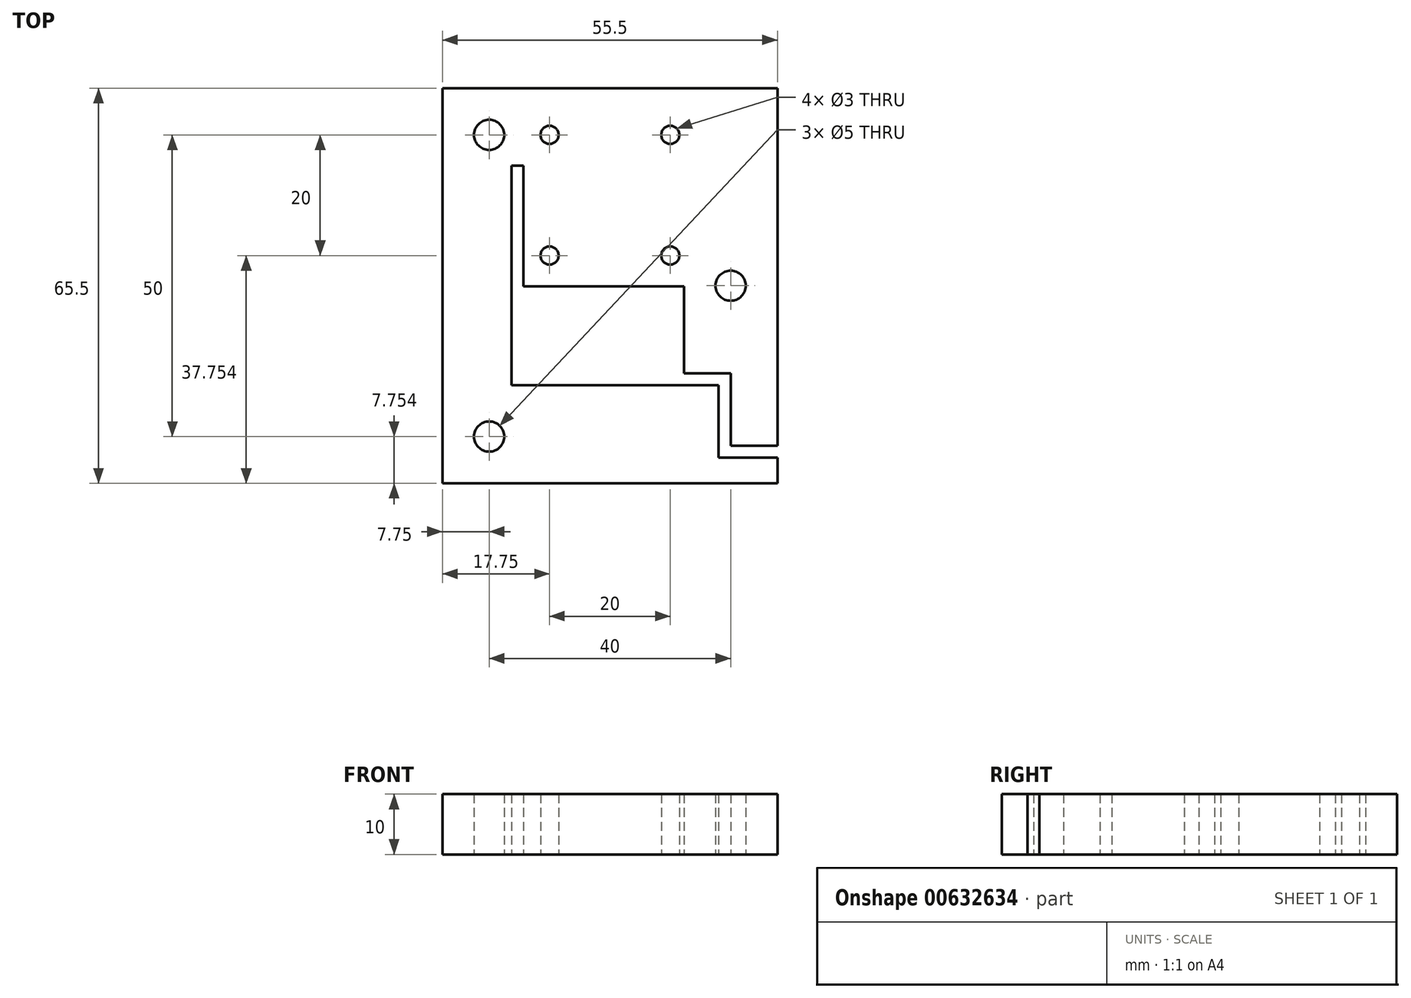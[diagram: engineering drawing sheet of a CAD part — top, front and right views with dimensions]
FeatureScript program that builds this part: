
annotation { "Feature Type Name" : "Feature", "Feature Type Description" : "" }
export const myFeature = defineFeature(function(context is Context, id is Id, definition is map)
    precondition{}
    {
        {
            var Q0;
            Q0=qCreatedBy(makeId("Top.planeOp"),FACE);
            var sketch = newSketch(context, id + "F0", { "sketchPlane" : qUnion([Q0])});
            skCircle(sketch, "E0", {"center": v(-20, 10.17) * mm, "radius": 2.5 * mm});
            skCircle(sketch, "E1", {"center": v(-20, -39.83) * mm, "radius": 2.5 * mm});
            skCircle(sketch, "E2", {"center": v(20, -14.83) * mm, "radius": 2.5 * mm});
            skCircle(sketch, "E3", {"center": v(-10, 10.17) * mm, "radius": 1.5 * mm});
            skCircle(sketch, "E4", {"center": v(-10, -9.83) * mm, "radius": 1.5 * mm});
            skCircle(sketch, "E5", {"center": v(10, 10.17) * mm, "radius": 1.5 * mm});
            skCircle(sketch, "E6", {"center": v(10, -9.83) * mm, "radius": 1.5 * mm});
            skLineSegment(sketch, "E7", {"start": v(-10, 10.17) * mm, "end": v(10, -9.83) * mm, "construction": true});
            skLineSegment(sketch, "E8", {"start": v(10, 10.17) * mm, "end": v(-10, -9.83) * mm, "construction": true});
            skPoint(sketch, "E9", {"position": v(0, 0.17) * mm});
            skLineSegment(sketch, "E10", {"start": v(95.55, 0.17) * mm, "end": v(-69.8, 0.17) * mm, "construction": true});
            skPoint(sketch, "E11.endSnap0", {"position": v(-34.9, 0.17) * mm});
            skLineSegment(sketch, "E12.bottom", {"start": v(-27.75, 17.92) * mm, "end": v(27.75, 17.92) * mm});
            skLineSegment(sketch, "E12.top", {"start": v(-27.75, -47.58) * mm, "end": v(27.75, -47.58) * mm});
            skLineSegment(sketch, "E12.left", {"start": v(-27.75, 17.92) * mm, "end": v(-27.75, -47.58) * mm});
            skLineSegment(sketch, "E12.right", {"start": v(27.75, 17.92) * mm, "end": v(27.75, -47.58) * mm});
            skLineSegment(sketch, "E13.bottom", {"start": v(-14.32, 5.08) * mm, "end": v(3.73, 5.08) * mm});
            skLineSegment(sketch, "E13.top", {"start": v(-12.5, -31.33) * mm, "end": v(18, -31.33) * mm});
            skLineSegment(sketch, "E13.right", {"start": v(3.73, 5.08) * mm, "end": v(3.73, -31.33) * mm});
            skLineSegment(sketch, "E14", {"start": v(18, -31.33) * mm, "end": v(18, -43.33) * mm});
            skLineSegment(sketch, "E15", {"start": v(18, -43.33) * mm, "end": v(27.75, -43.33) * mm});
            skLineSegment(sketch, "E16.0", {"start": v(20, -41.33) * mm, "end": v(27.75, -41.33) * mm});
            skLineSegment(sketch, "E16.1", {"start": v(20, -29.33) * mm, "end": v(20, -41.33) * mm});
            skLineSegment(sketch, "E16.2", {"start": v(-14.33, -29.33) * mm, "end": v(20, -29.33) * mm});
            skLineSegment(sketch, "E17.0", {"start": v(-16.32, 5.08) * mm, "end": v(-16.33, -31.33) * mm});
            skLineSegment(sketch, "E18", {"start": v(-16.33, -31.33) * mm, "end": v(-12.5, -31.33) * mm});
            skLineSegment(sketch, "E19", {"start": v(-16.32, 5.08) * mm, "end": v(-14.32, 5.08) * mm});
            skLineSegment(sketch, "E20", {"start": v(-14.33, -14.92) * mm, "end": v(12.25, -14.92) * mm});
            skLineSegment(sketch, "E21", {"start": v(12.25, -14.92) * mm, "end": v(12.25, -29.33) * mm});
            skCircle(sketch, "E22.cCircle", {"center": v(20, -14.83) * mm, "radius": 4 * mm, "construction": true});
            skLineSegment(sketch, "E22.0", {"start": v(24, -12.52) * mm, "end": v(24, -17.14) * mm});
            skLineSegment(sketch, "E22.1", {"start": v(24, -17.14) * mm, "end": v(20, -19.44) * mm});
            skLineSegment(sketch, "E22.2", {"start": v(20, -19.44) * mm, "end": v(16, -17.14) * mm});
            skLineSegment(sketch, "E22.3", {"start": v(16, -17.14) * mm, "end": v(16, -12.52) * mm});
            skLineSegment(sketch, "E22.4", {"start": v(16, -12.52) * mm, "end": v(20, -10.2) * mm});
            skLineSegment(sketch, "E22.5", {"start": v(20, -10.2) * mm, "end": v(24, -12.52) * mm});
            skPoint(sketch, "E22.0.midPoint", {"position": v(24, -14.83) * mm});
            skCircle(sketch, "E23.cCircle", {"center": v(-20, 10.17) * mm, "radius": 4 * mm, "construction": true});
            skLineSegment(sketch, "E23.0", {"start": v(-16, 12.48) * mm, "end": v(-16, 7.86) * mm});
            skLineSegment(sketch, "E23.1", {"start": v(-16, 7.86) * mm, "end": v(-20, 5.56) * mm});
            skLineSegment(sketch, "E23.2", {"start": v(-20, 5.56) * mm, "end": v(-24, 7.86) * mm});
            skLineSegment(sketch, "E23.3", {"start": v(-24, 7.86) * mm, "end": v(-24, 12.48) * mm});
            skLineSegment(sketch, "E23.4", {"start": v(-24, 12.48) * mm, "end": v(-20, 14.8) * mm});
            skLineSegment(sketch, "E23.5", {"start": v(-20, 14.8) * mm, "end": v(-16, 12.48) * mm});
            skCircle(sketch, "E24.cCircle", {"center": v(-20, -39.83) * mm, "radius": 4 * mm, "construction": true});
            skLineSegment(sketch, "E24.0", {"start": v(-16, -37.52) * mm, "end": v(-16, -42.14) * mm});
            skLineSegment(sketch, "E24.1", {"start": v(-16, -42.14) * mm, "end": v(-20, -44.44) * mm});
            skLineSegment(sketch, "E24.2", {"start": v(-20, -44.44) * mm, "end": v(-24, -42.14) * mm});
            skLineSegment(sketch, "E24.3", {"start": v(-24, -42.14) * mm, "end": v(-24, -37.52) * mm});
            skLineSegment(sketch, "E24.4", {"start": v(-24, -37.52) * mm, "end": v(-20, -35.2) * mm});
            skLineSegment(sketch, "E24.5", {"start": v(-20, -35.2) * mm, "end": v(-16, -37.52) * mm});
            skCircle(sketch, "E25.cCircle", {"center": v(-10, 10.17) * mm, "radius": 2.83 * mm, "construction": true});
            skLineSegment(sketch, "E25.0", {"start": v(-7.18, 11.8) * mm, "end": v(-7.18, 8.54) * mm});
            skLineSegment(sketch, "E25.1", {"start": v(-7.18, 8.54) * mm, "end": v(-10, 6.91) * mm});
            skLineSegment(sketch, "E25.2", {"start": v(-10, 6.91) * mm, "end": v(-12.83, 8.54) * mm});
            skLineSegment(sketch, "E25.3", {"start": v(-12.83, 8.54) * mm, "end": v(-12.83, 11.8) * mm});
            skLineSegment(sketch, "E25.4", {"start": v(-12.83, 11.8) * mm, "end": v(-10, 13.44) * mm});
            skLineSegment(sketch, "E25.5", {"start": v(-10, 13.44) * mm, "end": v(-7.18, 11.8) * mm});
            skCircle(sketch, "E26.cCircle", {"center": v(10, 10.17) * mm, "radius": 2.83 * mm, "construction": true});
            skLineSegment(sketch, "E26.0", {"start": v(12.82, 11.8) * mm, "end": v(12.82, 8.54) * mm});
            skLineSegment(sketch, "E26.1", {"start": v(12.82, 8.54) * mm, "end": v(10, 6.91) * mm});
            skLineSegment(sketch, "E26.2", {"start": v(10, 6.91) * mm, "end": v(7.17, 8.54) * mm});
            skLineSegment(sketch, "E26.3", {"start": v(7.17, 8.54) * mm, "end": v(7.17, 11.8) * mm});
            skLineSegment(sketch, "E26.4", {"start": v(7.17, 11.8) * mm, "end": v(10, 13.44) * mm});
            skLineSegment(sketch, "E26.5", {"start": v(10, 13.44) * mm, "end": v(12.82, 11.8) * mm});
            skCircle(sketch, "E27.cCircle", {"center": v(-10, -9.83) * mm, "radius": 2.83 * mm, "construction": true});
            skLineSegment(sketch, "E27.0", {"start": v(-7.18, -8.2) * mm, "end": v(-7.18, -11.46) * mm});
            skLineSegment(sketch, "E27.1", {"start": v(-7.18, -11.46) * mm, "end": v(-10, -13.09) * mm});
            skLineSegment(sketch, "E27.2", {"start": v(-10, -13.09) * mm, "end": v(-12.83, -11.46) * mm});
            skLineSegment(sketch, "E27.3", {"start": v(-12.82, -11.46) * mm, "end": v(-12.82, -8.2) * mm});
            skLineSegment(sketch, "E27.4", {"start": v(-12.82, -8.2) * mm, "end": v(-10, -6.56) * mm});
            skLineSegment(sketch, "E27.5", {"start": v(-10, -6.56) * mm, "end": v(-7.18, -8.2) * mm});
            skCircle(sketch, "E28.cCircle", {"center": v(10, -9.83) * mm, "radius": 2.83 * mm, "construction": true});
            skLineSegment(sketch, "E28.0", {"start": v(12.82, -8.2) * mm, "end": v(12.82, -11.46) * mm});
            skLineSegment(sketch, "E28.1", {"start": v(12.82, -11.46) * mm, "end": v(10, -13.09) * mm});
            skLineSegment(sketch, "E28.2", {"start": v(10, -13.09) * mm, "end": v(7.17, -11.46) * mm});
            skLineSegment(sketch, "E28.3", {"start": v(7.17, -11.46) * mm, "end": v(7.17, -8.2) * mm});
            skLineSegment(sketch, "E28.4", {"start": v(7.17, -8.2) * mm, "end": v(10, -6.56) * mm});
            skLineSegment(sketch, "E28.5", {"start": v(10, -6.56) * mm, "end": v(12.82, -8.2) * mm});
            skLineSegment(sketch, "E29.0", {"start": v(-14.32, 5.08) * mm, "end": v(-14.33, -31.33) * mm});
            skSolve(sketch);
        }
        {
            var Q0;
            {var subQ12=sQuery(id+"F0.wireOp",EDGE,"E12.bottom");Q0=makeQuery(id+"F0.imprint","IMPRINT",FACE,{"disambiguationData":[TD([[makeQuery(id+"F0.imprint","IMPRINT",EDGE,{"derivedFrom":subQ12}),-1.0]])]});}
            var Q1;
            {var subQ5=sQuery(id+"F0.wireOp",EDGE,"E13.bottom");Q1=makeQuery(id+"F0.imprint","IMPRINT",FACE,{"disambiguationData":[TD([[makeQuery(id+"F0.imprint","IMPRINT",EDGE,{"derivedFrom":subQ5}),-1.0]])]});}
            var Q2;
            Q2=makeQuery(id+"F0.imprint","IMPRINT",FACE,{"disambiguationData":[TD([[makeQuery(id+"F0.imprint","IMPRINT",EDGE,{"derivedFrom":sQuery(id+"F0.wireOp",EDGE,"E4")}),-1.0]])]});
            var Q3;
            Q3=makeQuery(id+"F0.imprint","IMPRINT",FACE,{"disambiguationData":[TD([[makeQuery(id+"F0.imprint","IMPRINT",EDGE,{"derivedFrom":sQuery(id+"F0.wireOp",EDGE,"E6")}),-1.0]])]});
            var Q4;
            Q4=makeQuery(id+"F0.imprint","IMPRINT",FACE,{"disambiguationData":[TD([[makeQuery(id+"F0.imprint","IMPRINT",EDGE,{"derivedFrom":sQuery(id+"F0.wireOp",EDGE,"E2")}),-1.0]])]});
            var Q5;
            Q5=makeQuery(id+"F0.imprint","IMPRINT",FACE,{"disambiguationData":[TD([[makeQuery(id+"F0.imprint","IMPRINT",EDGE,{"derivedFrom":sQuery(id+"F0.wireOp",EDGE,"E5")}),-1.0]])]});
            var Q6;
            Q6=makeQuery(id+"F0.imprint","IMPRINT",FACE,{"disambiguationData":[TD([[makeQuery(id+"F0.imprint","IMPRINT",EDGE,{"derivedFrom":sQuery(id+"F0.wireOp",EDGE,"E3")}),-1.0]])]});
            var Q7;
            Q7=makeQuery(id+"F0.imprint","IMPRINT",FACE,{"disambiguationData":[TD([[makeQuery(id+"F0.imprint","IMPRINT",EDGE,{"derivedFrom":sQuery(id+"F0.wireOp",EDGE,"E0")}),-1.0]])]});
            var Q8;
            Q8=makeQuery(id+"F0.imprint","IMPRINT",FACE,{"disambiguationData":[TD([[makeQuery(id+"F0.imprint","IMPRINT",EDGE,{"derivedFrom":sQuery(id+"F0.wireOp",EDGE,"E1")}),-1.0]])]});
            extrude(context, id + "F1", {"entities" : qUnion([Q0, Q1, Q2, Q3, Q4, Q5, Q6, Q7, Q8]), "depth" : 10 * mm, "offsetDistance" : 25 * mm});
        }
    });
